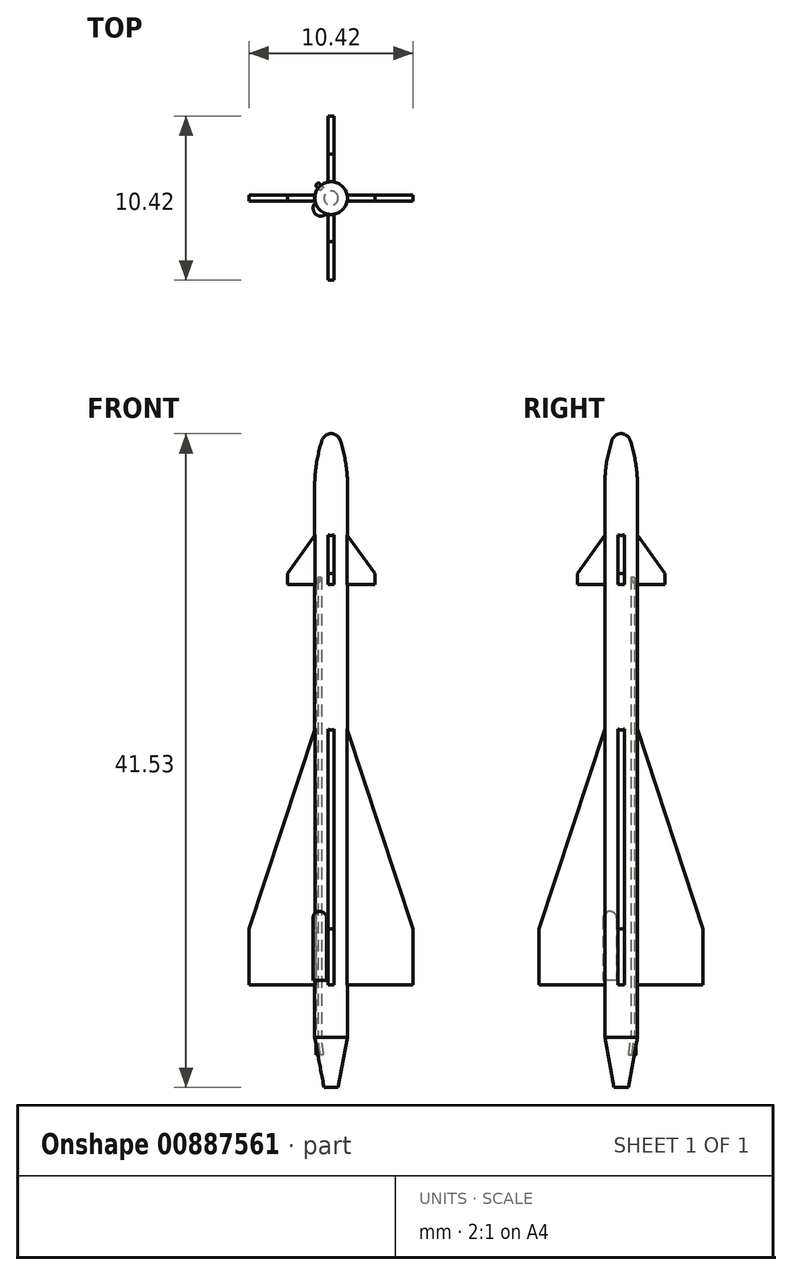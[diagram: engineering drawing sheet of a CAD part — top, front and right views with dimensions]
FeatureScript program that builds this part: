
annotation { "Feature Type Name" : "Feature", "Feature Type Description" : "" }
export const myFeature = defineFeature(function(context is Context, id is Id, definition is map)
    precondition{}
    {
        {
            var Q0;
            Q0=qCreatedBy(makeId("Front.planeOp"),FACE);
            var sketch = newSketch(context, id + "F0", { "sketchPlane" : qUnion([Q0])});
            skLineSegment(sketch, "E0", {"start": v(0, 0) * mm, "end": v(0, 41.53) * mm});
            skLineSegment(sketch, "E1", {"start": v(1.04, 38.2) * mm, "end": v(1.04, 0) * mm});
            skLineSegment(sketch, "E2", {"start": v(1.04, 0) * mm, "end": v(0, 0) * mm});
            skArc(sketch, "E3", {"start": v(0.58, 41.11) * mm, "mid": v(0.36, 41.41) * mm, "end": v(0, 41.53) * mm});
            skArc(sketch, "E4", {"start": v(1.04, 38.2) * mm, "mid": v(0.92, 39.67) * mm, "end": v(0.58, 41.11) * mm});
            skLineSegment(sketch, "E5", {"start": v(0, 41.53) * mm, "end": v(12.43, 41.53) * mm, "construction": true});
            skLineSegment(sketch, "E6", {"start": v(0.45, 0) * mm, "end": v(1.04, 3.2) * mm});
            skSolve(sketch);
        }
        {
            var Q0;
            Q0=makeQuery(id+"F0.imprint","IMPRINT",FACE,{"disambiguationData":[TD([[makeQuery(id+"F0.imprint","IMPRINT",EDGE,{"derivedFrom":sQuery(id+"F0.wireOp",EDGE,"E0")}),-1.0]])]});
            var Q1;
            Q1=sQuery(id+"F0.wireOp",EDGE,"E0");
            revolve(context, id + "F1", {"surfaceOperationType" : NewSurfaceOperationType.NEW, "entities" : qUnion([Q0]), "axis" : qUnion([Q1]), "revolveType" : RevolveType.FULL});
        }
        {
            var Q0;
            Q0=qCreatedBy(makeId("Front.planeOp"),FACE);
            var sketch = newSketch(context, id + "F2", { "sketchPlane" : qUnion([Q0])});
            skLineSegment(sketch, "E7.0", {"start": v(1.04, 38.2) * mm, "end": v(-1.04, 38.2) * mm, "construction": true});
            skLineSegment(sketch, "E8", {"start": v(0, 6.53) * mm, "end": v(5.2, 6.53) * mm});
            skLineSegment(sketch, "E9", {"start": v(5.2, 6.53) * mm, "end": v(5.2, 10.07) * mm});
            skLineSegment(sketch, "E10", {"start": v(5.2, 10.07) * mm, "end": v(1.04, 22.7) * mm});
            skLineSegment(sketch, "E11", {"start": v(0.4, 24.65) * mm, "end": v(0.4, 31.94) * mm});
            skLineSegment(sketch, "E12", {"start": v(0.4, 31.94) * mm, "end": v(2.78, 31.94) * mm});
            skLineSegment(sketch, "E13", {"start": v(2.78, 31.94) * mm, "end": v(2.78, 32.64) * mm});
            skLineSegment(sketch, "E14", {"start": v(2.78, 32.64) * mm, "end": v(0, 36.53) * mm});
            skLineSegment(sketch, "E15", {"start": v(0, 36.53) * mm, "end": v(0, 6.53) * mm});
            skLineSegment(sketch, "E16", {"start": v(1.04, 38.2) * mm, "end": v(1.04, 0) * mm, "construction": true});
            skPoint(sketch, "E17", {"position": v(1.04, 6.53) * mm});
            skPoint(sketch, "E18", {"position": v(1.04, 35.07) * mm});
            skLineSegment(sketch, "E19", {"start": v(1.04, 22.7) * mm, "end": v(0.4, 24.65) * mm});
            skLineSegment(sketch, "E20", {"start": v(1.04, 3.2) * mm, "end": v(0.45, 0) * mm});
            skSolve(sketch);
        }
        {
            var Q0;
            Q0=qSketchRegion(id+"F2",true);
            extrude(context, id + "F3", {"entities" : qUnion([Q0]), "operationType" : NewBodyOperationType.ADD, "oppositeDirection" : true, "depth" : .4 * mm, "offsetDistance" : 25 * mm, "symmetric" : true});
        }
        {
            var Q0;
            Q0=makeQuery(id+"F1.opRevolve","SWEPT_BODY",BODY,{"disambiguationData":[OSD([sQuery(id+"F0.wireOp",EDGE,"E0"),sQuery(id+"F0.wireOp",EDGE,"E1"),sQuery(id+"F0.wireOp",EDGE,"E2"),sQuery(id+"F0.wireOp",EDGE,"h1jDSi8t-veb7-85qg-XgDk-6E8DmZjBuz4r")])]});
            var Q1;
            Q1=makeQuery(id+"F1.opRevolve","SWEPT_FACE",FACE,{"disambiguationData":[OSD([sQuery(id+"F0.wireOp",EDGE,"E1")])]});
            circularPattern(context, id + "F4", {"operationType" : NewBodyOperationType.ADD, "entities" : qUnion([Q0]), "axis" : qUnion([Q1]), "angle" : 360 * degree, "instanceCount" : 4, "equalSpace" : true, "computeTransformsWithoutBuiltin" : true});
        }
        {
            var Q0;
            Q0=qCreatedBy(makeId("Top.planeOp"),FACE);
            cPlane(context, id + "F5", {"entities" : qUnion([Q0]), "cplaneType" : CPlaneType.OFFSET, "offset" : (980 / 144) * mm, "width" : 150 * mm, "height" : 150 * mm});
        }
        {
            var Q0;
            Q0=qCreatedBy(id+"F5.planeOp",FACE);
            var sketch = newSketch(context, id + "F6", { "sketchPlane" : qUnion([Q0])});
            skLineSegment(sketch, "E21", {"start": v(-1, -0.3) * mm, "end": v(-0.7, 0) * mm});
            skLineSegment(sketch, "E22", {"start": v(-0.7, 0) * mm, "end": v(0, -0.7) * mm});
            skLineSegment(sketch, "E23", {"start": v(0, -0.7) * mm, "end": v(-0.3, -1) * mm});
            skArc(sketch, "E24", {"start": v(-1, -0.3) * mm, "mid": v(-1, -1) * mm, "end": v(-0.3, -1) * mm});
            skLineSegment(sketch, "E25", {"start": v(-0.35, -0.35) * mm, "end": v(0, 0) * mm, "construction": true});
            skLineSegment(sketch, "E26", {"start": v(0, 0) * mm, "end": v(-2.42, 0) * mm, "construction": true});
            skCircle(sketch, "E27.0", {"center": v(0, 0) * mm, "radius": 1.04 * mm});
            skSolve(sketch);
        }
        {
            var Q0;
            Q0 = qSketchRegion(id + "F6", true);
            extrude(context, id + "F7", {"entities" : qUnion([Q0]), "operationType" : NewBodyOperationType.ADD, "depth" : (630 / 144) * mm, "offsetDistance" : 25 * mm});
        }
        {
            var Q0;
            Q0=makeQuery(id+"F7.opExtrude","CAP_EDGE",EDGE,{"disambiguationData":[OSD([sQuery(id+"F6.wireOp",EDGE,"E24")])],"isStart":false});
            fillet(context, id + "F8", {"entities" : qUnion([Q0]), "radius" : .4 * mm, "tangentPropagation" : true, "allowEdgeOverflow" : false});
        }
        {
            var Q0;
            Q0=qCreatedBy(makeId("Top.planeOp"),FACE);
            cPlane(context, id + "F9", {"entities" : qUnion([Q0]), "cplaneType" : CPlaneType.OFFSET, "offset" : (300 / 144) * mm, "width" : 150 * mm, "height" : 150 * mm});
        }
        {
            var Q0;
            Q0=qCreatedBy(id+"F9.planeOp",FACE);
            var sketch = newSketch(context, id + "F10", { "sketchPlane" : qUnion([Q0])});
            skCircle(sketch, "E28.0", {"center": v(0, 0) * mm, "radius": 1.04 * mm});
            skLineSegment(sketch, "E29", {"start": v(-0.35, 0.14) * mm, "end": v(-0.14, 0.35) * mm});
            skLineSegment(sketch, "E30", {"start": v(-0.14, 0.35) * mm, "end": v(-0.7, 0.9) * mm});
            skLineSegment(sketch, "E31", {"start": v(-0.35, 0.14) * mm, "end": v(-0.9, 0.7) * mm});
            skLineSegment(sketch, "E32", {"start": v(0, 0) * mm, "end": v(-0.25, 0.25) * mm, "construction": true});
            skLineSegment(sketch, "E33", {"start": v(0, 0) * mm, "end": v(-0.55, 0) * mm, "construction": true});
            skArc(sketch, "E34", {"start": v(-0.7, 0.9) * mm, "mid": v(-0.9, 0.9) * mm, "end": v(-0.9, 0.7) * mm});
            skSolve(sketch);
        }
        {
            var Q0;
            {var subQ5=sQuery(id+"F10.wireOp",EDGE,"E29");Q0=makeQuery(id+"F10.imprint","IMPRINT",FACE,{"disambiguationData":[TD([[makeQuery(id+"F10.imprint","IMPRINT",EDGE,{"derivedFrom":subQ5}),1.0]])]});}
            var Q1;
            {var subQ5=sQuery(id+"F10.wireOp",EDGE,"E34");Q1=makeQuery(id+"F10.imprint","IMPRINT",FACE,{"disambiguationData":[TD([[makeQuery(id+"F10.imprint","IMPRINT",EDGE,{"derivedFrom":subQ5}),1.0]])]});}
            extrude(context, id + "F11", {"entities" : qUnion([Q0, Q1]), "operationType" : NewBodyOperationType.ADD, "depth" : (4300 / 144) * mm, "offsetDistance" : 25 * mm});
        }
        {
            var Q0;
            Q0=makeQuery(id+"F11.boolean.opBoolean","INTERSECT",EDGE,{"derivedFrom":[makeQuery(id+"F1.opRevolve","SWEPT_FACE",FACE,{"disambiguationData":[OSD([sQuery(id+"F0.wireOp",EDGE,"E1")])]}),makeQuery(id+"F11.opExtrude","CAP_FACE",FACE,{"disambiguationData":[OSD([sQuery(id+"F10.wireOp",EDGE,"E29"),sQuery(id+"F10.wireOp",EDGE,"E30"),sQuery(id+"F10.wireOp",EDGE,"E31"),sQuery(id+"F10.wireOp",EDGE,"E34")])],"isStart":false})]});
            chamfer(context, id + "F12", {"entities" : qUnion([Q0]), "chamferType" : ChamferType.OFFSET_ANGLE, "width" : .25 * mm, "oppositeDirection" : true, "angle" : 60 * degree, "tangentPropagation" : true});
        }
    });
